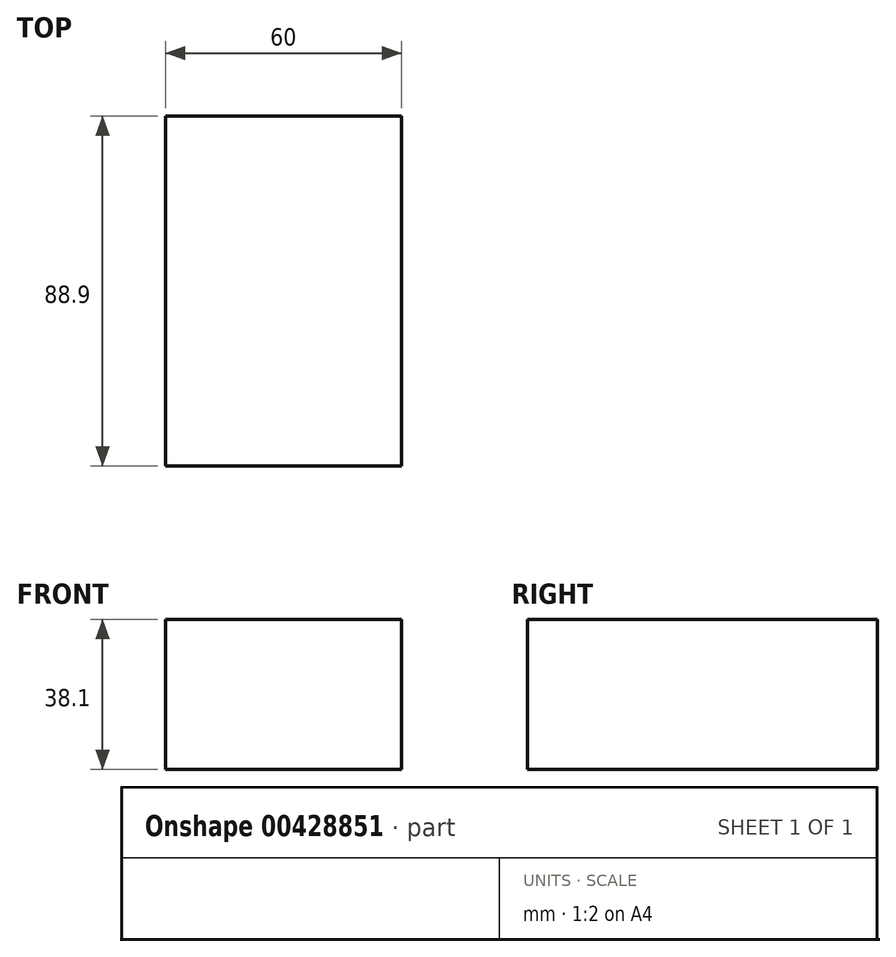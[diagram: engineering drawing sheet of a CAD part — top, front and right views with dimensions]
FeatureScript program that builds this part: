
annotation { "Feature Type Name" : "Feature", "Feature Type Description" : "" }
export const myFeature = defineFeature(function(context is Context, id is Id, definition is map)
    precondition{}
    {
        {
            assignVariable(context, id + "F0", {"name" : "Length", "anyValue" : 60});
        }
        {
            var Q0;
            Q0=qCreatedBy(makeId("Right.planeOp"),FACE);
            var sketch = newSketch(context, id + "F1", { "sketchPlane" : qUnion([Q0])});
            skLineSegment(sketch, "E0.bottom", {"start": v(44.45, -19.05) * mm, "end": v(-44.45, -19.05) * mm});
            skLineSegment(sketch, "E0.top", {"start": v(44.45, 19.05) * mm, "end": v(-44.45, 19.05) * mm});
            skLineSegment(sketch, "E0.left", {"start": v(44.45, -19.05) * mm, "end": v(44.45, 19.05) * mm});
            skLineSegment(sketch, "E0.right", {"start": v(-44.45, -19.05) * mm, "end": v(-44.45, 19.05) * mm});
            skPoint(sketch, "E0.middle", {"position": v(0, 0) * mm});
            skSolve(sketch);
        }
        {
            var Q0;
            Q0=makeQuery(id+"F1.imprint","IMPRINT",FACE,{"disambiguationData":[TD([[makeQuery(id+"F1.imprint","IMPRINT",EDGE,{"derivedFrom":sQuery(id+"F1.wireOp",EDGE,"E0.bottom")}),-1.0]])]});
            extrude(context, id + "F2", {"entities" : qUnion([Q0]), "depth" : (getVariable(context, 'Length')) * mm, "symmetric" : true});
        }
    });
